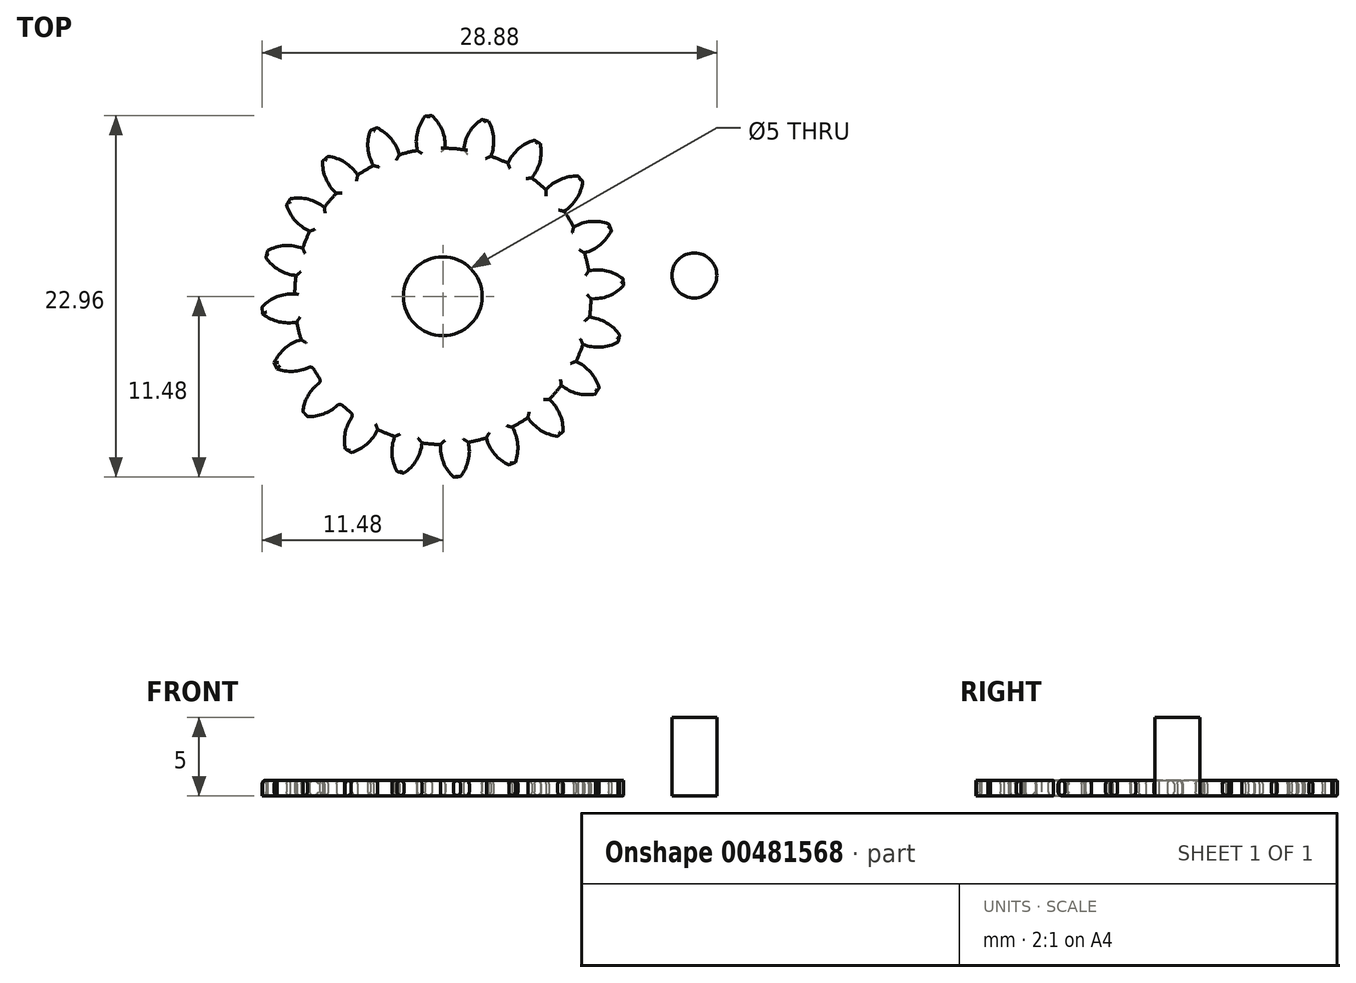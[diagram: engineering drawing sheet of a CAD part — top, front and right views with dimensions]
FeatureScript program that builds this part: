
annotation { "Feature Type Name" : "Feature", "Feature Type Description" : "" }
export const myFeature = defineFeature(function(context is Context, id is Id, definition is map)
    precondition{}
    {
        {
            assignVariable(context, id + "F0", {"name" : "GearDepth", "anyValue" : 1});
        }
        {
            assignVariable(context, id + "F1", {"name" : "TeethFillet", "anyValue" : getVariable(context, 'GearDepth') * .25});
        }
        {
            var Q0;
            Q0=qCreatedBy(makeId("Top.planeOp"),FACE);
            var sketch = newSketch(context, id + "F2", { "sketchPlane" : qUnion([Q0])});
            skCircle(sketch, "E0", {"center": v(0, 0) * mm, "radius": 9.4 * mm});
            skCircle(sketch, "E1", {"center": v(0, 0) * mm, "radius": 10.45 * mm, "construction": true});
            skCircle(sketch, "E2", {"center": v(0, 0) * mm, "radius": 11.5 * mm, "construction": true});
            skLineSegment(sketch, "E3", {"start": v(0, 0) * mm, "end": v(0, 17.6) * mm, "construction": true});
            skLineSegment(sketch, "E4", {"start": v(0, 0) * mm, "end": v(-1.42, 18) * mm, "construction": true});
            skLineSegment(sketch, "E5", {"start": v(0, 10.45) * mm, "end": v(-10.54, 10.45) * mm, "construction": true});
            skLineSegment(sketch, "E6", {"start": v(0, 10.45) * mm, "end": v(-10.3, 6.7) * mm, "construction": true});
            skCircle(sketch, "E7", {"center": v(0, 10.45) * mm, "radius": 2.61 * mm, "construction": true});
            skCircle(sketch, "E8", {"center": v(-2.46, 9.56) * mm, "radius": 2.61 * mm, "construction": true});
            skArc(sketch, "E9", {"start": v(-4.91, 10.45) * mm, "mid": v(-4.92, 10.42) * mm, "end": v(-4.94, 10.39) * mm});
            skArc(sketch, "E10.trimOffspring", {"start": v(0.15, 9.4) * mm, "mid": v(-0.03, 10.54) * mm, "end": v(-0.68, 11.48) * mm});
            skArc(sketch, "E11.MirrorCS", {"start": v(-1.62, 9.27) * mm, "mid": v(-1.62, 10.41) * mm, "end": v(-1.12, 11.45) * mm});
            skLineSegment(sketch, "E12", {"start": v(-1.12, 11.45) * mm, "end": v(-0.68, 11.48) * mm});
            skArc(sketch, "E13.1.0", {"start": v(-2.76, 9) * mm, "mid": v(-3.29, 10.01) * mm, "end": v(-4.2, 10.7) * mm});
            skLineSegment(sketch, "E13.1.1", {"start": v(-4.6, 10.54) * mm, "end": v(-4.2, 10.7) * mm});
            skArc(sketch, "E13.1.2", {"start": v(-4.4, 8.31) * mm, "mid": v(-4.76, 9.4) * mm, "end": v(-4.6, 10.54) * mm});
            skArc(sketch, "E13.2.0", {"start": v(-5.4, 7.7) * mm, "mid": v(-6.22, 8.5) * mm, "end": v(-7.3, 8.89) * mm});
            skLineSegment(sketch, "E13.2.1", {"start": v(-7.64, 8.6) * mm, "end": v(-7.3, 8.89) * mm});
            skArc(sketch, "E13.2.2", {"start": v(-6.76, 6.54) * mm, "mid": v(-7.43, 7.47) * mm, "end": v(-7.64, 8.6) * mm});
            skArc(sketch, "E13.3.0", {"start": v(-7.52, 5.65) * mm, "mid": v(-8.54, 6.17) * mm, "end": v(-9.69, 6.2) * mm});
            skLineSegment(sketch, "E13.3.1", {"start": v(-9.92, 5.82) * mm, "end": v(-9.69, 6.2) * mm});
            skArc(sketch, "E13.3.2", {"start": v(-8.45, 4.13) * mm, "mid": v(-9.37, 4.81) * mm, "end": v(-9.92, 5.82) * mm});
            skArc(sketch, "E13.4.0", {"start": v(-8.9, 3.05) * mm, "mid": v(-10.03, 3.23) * mm, "end": v(-11.13, 2.9) * mm});
            skLineSegment(sketch, "E13.4.1", {"start": v(-11.23, 2.47) * mm, "end": v(-11.13, 2.9) * mm});
            skArc(sketch, "E13.4.2", {"start": v(-9.32, 1.32) * mm, "mid": v(-10.4, 1.68) * mm, "end": v(-11.23, 2.47) * mm});
            skArc(sketch, "E13.5.0", {"start": v(-9.4, 0.15) * mm, "mid": v(-10.54, -0.03) * mm, "end": v(-11.48, -0.68) * mm});
            skLineSegment(sketch, "E13.5.1", {"start": v(-11.45, -1.12) * mm, "end": v(-11.48, -0.68) * mm});
            skArc(sketch, "E13.5.2", {"start": v(-9.27, -1.62) * mm, "mid": v(-10.41, -1.62) * mm, "end": v(-11.45, -1.12) * mm});
            skArc(sketch, "E13.6.0", {"start": v(-9, -2.76) * mm, "mid": v(-10.01, -3.29) * mm, "end": v(-10.7, -4.2) * mm});
            skLineSegment(sketch, "E13.6.1", {"start": v(-10.54, -4.6) * mm, "end": v(-10.7, -4.2) * mm});
            skArc(sketch, "E13.6.2", {"start": v(-8.31, -4.4) * mm, "mid": v(-9.4, -4.76) * mm, "end": v(-10.54, -4.6) * mm});
            skArc(sketch, "E13.7.0", {"start": v(-7.7, -5.4) * mm, "mid": v(-8.5, -6.22) * mm, "end": v(-8.89, -7.3) * mm});
            skLineSegment(sketch, "E13.7.1", {"start": v(-8.6, -7.64) * mm, "end": v(-8.89, -7.3) * mm});
            skArc(sketch, "E13.7.2", {"start": v(-6.54, -6.76) * mm, "mid": v(-7.47, -7.43) * mm, "end": v(-8.6, -7.64) * mm});
            skArc(sketch, "E13.8.0", {"start": v(-5.65, -7.52) * mm, "mid": v(-6.17, -8.54) * mm, "end": v(-6.2, -9.69) * mm});
            skLineSegment(sketch, "E13.8.1", {"start": v(-5.82, -9.92) * mm, "end": v(-6.2, -9.69) * mm});
            skArc(sketch, "E13.8.2", {"start": v(-4.13, -8.45) * mm, "mid": v(-4.81, -9.37) * mm, "end": v(-5.82, -9.92) * mm});
            skArc(sketch, "E13.9.0", {"start": v(-3.05, -8.9) * mm, "mid": v(-3.23, -10.03) * mm, "end": v(-2.9, -11.13) * mm});
            skLineSegment(sketch, "E13.9.1", {"start": v(-2.47, -11.23) * mm, "end": v(-2.9, -11.13) * mm});
            skArc(sketch, "E13.9.2", {"start": v(-1.32, -9.32) * mm, "mid": v(-1.68, -10.4) * mm, "end": v(-2.47, -11.23) * mm});
            skArc(sketch, "E13.10.0", {"start": v(-0.15, -9.4) * mm, "mid": v(0.03, -10.54) * mm, "end": v(0.68, -11.48) * mm});
            skLineSegment(sketch, "E13.10.1", {"start": v(1.12, -11.45) * mm, "end": v(0.68, -11.48) * mm});
            skArc(sketch, "E13.10.2", {"start": v(1.62, -9.27) * mm, "mid": v(1.62, -10.41) * mm, "end": v(1.12, -11.45) * mm});
            skArc(sketch, "E13.11.0", {"start": v(2.76, -9) * mm, "mid": v(3.29, -10.01) * mm, "end": v(4.2, -10.7) * mm});
            skLineSegment(sketch, "E13.11.1", {"start": v(4.6, -10.54) * mm, "end": v(4.2, -10.7) * mm});
            skArc(sketch, "E13.11.2", {"start": v(4.4, -8.31) * mm, "mid": v(4.76, -9.4) * mm, "end": v(4.6, -10.54) * mm});
            skArc(sketch, "E13.12.0", {"start": v(5.4, -7.7) * mm, "mid": v(6.22, -8.5) * mm, "end": v(7.3, -8.89) * mm});
            skLineSegment(sketch, "E13.12.1", {"start": v(7.64, -8.6) * mm, "end": v(7.3, -8.89) * mm});
            skArc(sketch, "E13.12.2", {"start": v(6.76, -6.54) * mm, "mid": v(7.43, -7.47) * mm, "end": v(7.64, -8.6) * mm});
            skArc(sketch, "E13.13.0", {"start": v(7.52, -5.65) * mm, "mid": v(8.54, -6.17) * mm, "end": v(9.69, -6.2) * mm});
            skLineSegment(sketch, "E13.13.1", {"start": v(9.92, -5.82) * mm, "end": v(9.69, -6.2) * mm});
            skArc(sketch, "E13.13.2", {"start": v(8.45, -4.13) * mm, "mid": v(9.37, -4.81) * mm, "end": v(9.92, -5.82) * mm});
            skArc(sketch, "E13.14.0", {"start": v(8.9, -3.05) * mm, "mid": v(10.03, -3.23) * mm, "end": v(11.13, -2.9) * mm});
            skLineSegment(sketch, "E13.14.1", {"start": v(11.23, -2.47) * mm, "end": v(11.13, -2.9) * mm});
            skArc(sketch, "E13.14.2", {"start": v(9.32, -1.32) * mm, "mid": v(10.4, -1.68) * mm, "end": v(11.23, -2.47) * mm});
            skArc(sketch, "E13.15.0", {"start": v(9.4, -0.15) * mm, "mid": v(10.54, 0.03) * mm, "end": v(11.48, 0.68) * mm});
            skLineSegment(sketch, "E13.15.1", {"start": v(11.45, 1.12) * mm, "end": v(11.48, 0.68) * mm});
            skArc(sketch, "E13.15.2", {"start": v(9.27, 1.62) * mm, "mid": v(10.41, 1.62) * mm, "end": v(11.45, 1.12) * mm});
            skArc(sketch, "E13.16.0", {"start": v(9, 2.76) * mm, "mid": v(10.01, 3.29) * mm, "end": v(10.7, 4.2) * mm});
            skLineSegment(sketch, "E13.16.1", {"start": v(10.54, 4.6) * mm, "end": v(10.7, 4.2) * mm});
            skArc(sketch, "E13.16.2", {"start": v(8.31, 4.4) * mm, "mid": v(9.4, 4.76) * mm, "end": v(10.54, 4.6) * mm});
            skArc(sketch, "E13.17.0", {"start": v(7.7, 5.4) * mm, "mid": v(8.5, 6.22) * mm, "end": v(8.89, 7.3) * mm});
            skLineSegment(sketch, "E13.17.1", {"start": v(8.6, 7.64) * mm, "end": v(8.89, 7.3) * mm});
            skArc(sketch, "E13.17.2", {"start": v(6.54, 6.76) * mm, "mid": v(7.47, 7.43) * mm, "end": v(8.6, 7.64) * mm});
            skArc(sketch, "E13.18.0", {"start": v(5.65, 7.52) * mm, "mid": v(6.17, 8.54) * mm, "end": v(6.2, 9.69) * mm});
            skLineSegment(sketch, "E13.18.1", {"start": v(5.82, 9.92) * mm, "end": v(6.2, 9.69) * mm});
            skArc(sketch, "E13.18.2", {"start": v(4.13, 8.45) * mm, "mid": v(4.81, 9.37) * mm, "end": v(5.82, 9.92) * mm});
            skArc(sketch, "E13.19.0", {"start": v(3.05, 8.9) * mm, "mid": v(3.23, 10.03) * mm, "end": v(2.9, 11.13) * mm});
            skLineSegment(sketch, "E13.19.1", {"start": v(2.47, 11.23) * mm, "end": v(2.9, 11.13) * mm});
            skArc(sketch, "E13.19.2", {"start": v(1.32, 9.32) * mm, "mid": v(1.68, 10.4) * mm, "end": v(2.47, 11.23) * mm});
            skCircle(sketch, "E14", {"center": v(0, 0) * mm, "radius": 2.5 * mm});
            skSolve(sketch);
        }
        {
            var Q0;
            {var subQ0=sQuery(id+"F2.wireOp",EDGE,"E10.trimOffspring");Q0=makeQuery(id+"F2.imprint","IMPRINT",FACE,{"disambiguationData":[TD([[makeQuery(id+"F2.imprint","IMPRINT",EDGE,{"derivedFrom":subQ0}),1.0]])]});}
            var Q1;
            {var subQ0=sQuery(id+"F2.wireOp",EDGE,"E0");var subQ1=makeQuery(id+"F2.imprint","INTERSECT",VERTEX,{"derivedFrom":[subQ0,sQuery(id+"F2.wireOp",EDGE,"E10.trimOffspring")]});Q1=makeQuery(id+"F2.imprint","IMPRINT",FACE,{"disambiguationData":[TD([[makeQuery(id+"F2.imprint","IMPRINT",EDGE,{"disambiguationData":[TD([[subQ1,-1.0]])],"derivedFrom":subQ0}),1.0]])]});}
            var Q2;
            {var subQ0=sQuery(id+"F2.wireOp",EDGE,"E13.1.0");Q2=makeQuery(id+"F2.imprint","IMPRINT",FACE,{"disambiguationData":[TD([[makeQuery(id+"F2.imprint","IMPRINT",EDGE,{"derivedFrom":subQ0}),1.0]])]});}
            var Q3;
            {var subQ0=sQuery(id+"F2.wireOp",EDGE,"E13.2.0");Q3=makeQuery(id+"F2.imprint","IMPRINT",FACE,{"disambiguationData":[TD([[makeQuery(id+"F2.imprint","IMPRINT",EDGE,{"derivedFrom":subQ0}),1.0]])]});}
            var Q4;
            {var subQ0=sQuery(id+"F2.wireOp",EDGE,"E13.3.0");Q4=makeQuery(id+"F2.imprint","IMPRINT",FACE,{"disambiguationData":[TD([[makeQuery(id+"F2.imprint","IMPRINT",EDGE,{"derivedFrom":subQ0}),1.0]])]});}
            var Q5;
            {var subQ0=sQuery(id+"F2.wireOp",EDGE,"E13.4.0");Q5=makeQuery(id+"F2.imprint","IMPRINT",FACE,{"disambiguationData":[TD([[makeQuery(id+"F2.imprint","IMPRINT",EDGE,{"derivedFrom":subQ0}),1.0]])]});}
            var Q6;
            {var subQ0=sQuery(id+"F2.wireOp",EDGE,"E13.5.0");Q6=makeQuery(id+"F2.imprint","IMPRINT",FACE,{"disambiguationData":[TD([[makeQuery(id+"F2.imprint","IMPRINT",EDGE,{"derivedFrom":subQ0}),1.0]])]});}
            var Q7;
            {var subQ0=sQuery(id+"F2.wireOp",EDGE,"E13.6.0");Q7=makeQuery(id+"F2.imprint","IMPRINT",FACE,{"disambiguationData":[TD([[makeQuery(id+"F2.imprint","IMPRINT",EDGE,{"derivedFrom":subQ0}),1.0]])]});}
            var Q8;
            {var subQ0=sQuery(id+"F2.wireOp",EDGE,"E13.7.0");Q8=makeQuery(id+"F2.imprint","IMPRINT",FACE,{"disambiguationData":[TD([[makeQuery(id+"F2.imprint","IMPRINT",EDGE,{"derivedFrom":subQ0}),1.0]])]});}
            var Q9;
            {var subQ0=sQuery(id+"F2.wireOp",EDGE,"E13.8.0");Q9=makeQuery(id+"F2.imprint","IMPRINT",FACE,{"disambiguationData":[TD([[makeQuery(id+"F2.imprint","IMPRINT",EDGE,{"derivedFrom":subQ0}),1.0]])]});}
            var Q10;
            {var subQ0=sQuery(id+"F2.wireOp",EDGE,"E13.9.0");Q10=makeQuery(id+"F2.imprint","IMPRINT",FACE,{"disambiguationData":[TD([[makeQuery(id+"F2.imprint","IMPRINT",EDGE,{"derivedFrom":subQ0}),1.0]])]});}
            var Q11;
            {var subQ0=sQuery(id+"F2.wireOp",EDGE,"E13.10.0");Q11=makeQuery(id+"F2.imprint","IMPRINT",FACE,{"disambiguationData":[TD([[makeQuery(id+"F2.imprint","IMPRINT",EDGE,{"derivedFrom":subQ0}),1.0]])]});}
            var Q12;
            {var subQ0=sQuery(id+"F2.wireOp",EDGE,"E13.11.0");Q12=makeQuery(id+"F2.imprint","IMPRINT",FACE,{"disambiguationData":[TD([[makeQuery(id+"F2.imprint","IMPRINT",EDGE,{"derivedFrom":subQ0}),1.0]])]});}
            var Q13;
            {var subQ0=sQuery(id+"F2.wireOp",EDGE,"E13.12.0");Q13=makeQuery(id+"F2.imprint","IMPRINT",FACE,{"disambiguationData":[TD([[makeQuery(id+"F2.imprint","IMPRINT",EDGE,{"derivedFrom":subQ0}),1.0]])]});}
            var Q14;
            {var subQ0=sQuery(id+"F2.wireOp",EDGE,"E13.13.0");Q14=makeQuery(id+"F2.imprint","IMPRINT",FACE,{"disambiguationData":[TD([[makeQuery(id+"F2.imprint","IMPRINT",EDGE,{"derivedFrom":subQ0}),1.0]])]});}
            var Q15;
            {var subQ0=sQuery(id+"F2.wireOp",EDGE,"E13.14.0");Q15=makeQuery(id+"F2.imprint","IMPRINT",FACE,{"disambiguationData":[TD([[makeQuery(id+"F2.imprint","IMPRINT",EDGE,{"derivedFrom":subQ0}),1.0]])]});}
            var Q16;
            {var subQ0=sQuery(id+"F2.wireOp",EDGE,"E13.15.0");Q16=makeQuery(id+"F2.imprint","IMPRINT",FACE,{"disambiguationData":[TD([[makeQuery(id+"F2.imprint","IMPRINT",EDGE,{"derivedFrom":subQ0}),1.0]])]});}
            var Q17;
            {var subQ0=sQuery(id+"F2.wireOp",EDGE,"E13.16.0");Q17=makeQuery(id+"F2.imprint","IMPRINT",FACE,{"disambiguationData":[TD([[makeQuery(id+"F2.imprint","IMPRINT",EDGE,{"derivedFrom":subQ0}),1.0]])]});}
            var Q18;
            {var subQ0=sQuery(id+"F2.wireOp",EDGE,"E13.17.0");Q18=makeQuery(id+"F2.imprint","IMPRINT",FACE,{"disambiguationData":[TD([[makeQuery(id+"F2.imprint","IMPRINT",EDGE,{"derivedFrom":subQ0}),1.0]])]});}
            var Q19;
            {var subQ0=sQuery(id+"F2.wireOp",EDGE,"E13.18.0");Q19=makeQuery(id+"F2.imprint","IMPRINT",FACE,{"disambiguationData":[TD([[makeQuery(id+"F2.imprint","IMPRINT",EDGE,{"derivedFrom":subQ0}),1.0]])]});}
            var Q20;
            {var subQ0=sQuery(id+"F2.wireOp",EDGE,"E13.19.0");Q20=makeQuery(id+"F2.imprint","IMPRINT",FACE,{"disambiguationData":[TD([[makeQuery(id+"F2.imprint","IMPRINT",EDGE,{"derivedFrom":subQ0}),1.0]])]});}
            var Q21;
            Q21=sQuery(id+"F2.wireOp",EDGE,"E0");
            var Q22;
            Q22=sQuery(id+"F2.wireOp",EDGE,"E10.trimOffspring");
            var Q23;
            Q23=sQuery(id+"F2.wireOp",EDGE,"E12");
            var Q24;
            Q24=sQuery(id+"F2.wireOp",EDGE,"E11.MirrorCS");
            extrude(context, id + "F3", {"entities" : qUnion([Q0, Q1, Q2, Q3, Q4, Q5, Q6, Q7, Q8, Q9, Q10, Q11, Q12, Q13, Q14, Q15, Q16, Q17, Q18, Q19, Q20]), "surfaceEntities" : qUnion([Q21, Q22, Q23, Q24]), "depth" : (getVariable(context, 'GearDepth')) * mm});
        }
        {
            var Q0;
            Q0=qCreatedBy(makeId("Top.planeOp"),FACE);
            var sketch = newSketch(context, id + "F4", { "sketchPlane" : qUnion([Q0])});
            skCircle(sketch, "E15", {"center": v(15.97, 1.33) * mm, "radius": 1.43 * mm});
            skSolve(sketch);
        }
        {
            var Q0;
            Q0=makeQuery(id+"F4.imprint","IMPRINT",FACE,{"disambiguationData":[TD([[makeQuery(id+"F4.imprint","IMPRINT",EDGE,{"derivedFrom":sQuery(id+"F4.wireOp",EDGE,"E15")}),1.0]])]});
            extrude(context, id + "F5", {"entities" : qUnion([Q0]), "depth" : 5 * mm});
        }
        {
            var Q0;
            Q0=makeQuery(id+"F3.opExtrude","CAP_EDGE",EDGE,{"disambiguationData":[OSD([sQuery(id+"F2.wireOp",EDGE,"E13.5.2")])],"isStart":false});
            var Q1;
            Q1=makeQuery(id+"F3.opExtrude","CAP_EDGE",EDGE,{"disambiguationData":[OSD([sQuery(id+"F2.wireOp",EDGE,"E13.5.1")])],"isStart":false});
            var Q2;
            {var subQ0=sQuery(id+"F2.wireOp",EDGE,"E0");Q2=makeQuery(id+"F3.opExtrude","CAP_EDGE",EDGE,{"disambiguationData":[OSD([subQ0]),TDD([makeQuery(id+"F2.imprint","IMPRINT",EDGE,{"disambiguationData":[TD([[makeQuery(id+"F2.imprint","INTERSECT",VERTEX,{"derivedFrom":[subQ0,sQuery(id+"F2.wireOp",EDGE,"E13.5.2")]}),-1.0]])],"derivedFrom":subQ0})])],"isStart":false});}
            var Q3;
            Q3=makeQuery(id+"F3.opExtrude","CAP_EDGE",EDGE,{"disambiguationData":[OSD([sQuery(id+"F2.wireOp",EDGE,"E13.6.0")])],"isStart":false});
            var Q4;
            Q4=makeQuery(id+"F3.opExtrude","CAP_EDGE",EDGE,{"disambiguationData":[OSD([sQuery(id+"F2.wireOp",EDGE,"E13.6.1")])],"isStart":false});
            var Q5;
            Q5=makeQuery(id+"F3.opExtrude","CAP_EDGE",EDGE,{"disambiguationData":[OSD([sQuery(id+"F2.wireOp",EDGE,"E13.6.2")])],"isStart":false});
            var Q6;
            {var subQ0=sQuery(id+"F2.wireOp",EDGE,"E0");Q6=makeQuery(id+"F3.opExtrude","SWEPT_FACE",FACE,{"disambiguationData":[OSD([subQ0]),TDD([makeQuery(id+"F2.imprint","IMPRINT",EDGE,{"disambiguationData":[TD([[makeQuery(id+"F2.imprint","INTERSECT",VERTEX,{"derivedFrom":[subQ0,sQuery(id+"F2.wireOp",EDGE,"E13.6.2")]}),-1.0]])],"derivedFrom":subQ0})])]});}
            var Q7;
            {var subQ0=sQuery(id+"F2.wireOp",EDGE,"E0");Q7=makeQuery(id+"F3.opExtrude","CAP_EDGE",EDGE,{"disambiguationData":[OSD([subQ0]),TDD([makeQuery(id+"F2.imprint","IMPRINT",EDGE,{"disambiguationData":[TD([[makeQuery(id+"F2.imprint","INTERSECT",VERTEX,{"derivedFrom":[subQ0,sQuery(id+"F2.wireOp",EDGE,"E13.6.2")]}),-1.0]])],"derivedFrom":subQ0})])],"isStart":false});}
            var Q8;
            Q8=makeQuery(id+"F3.opExtrude","CAP_EDGE",EDGE,{"disambiguationData":[OSD([sQuery(id+"F2.wireOp",EDGE,"E13.7.2")])],"isStart":true});
            var Q9;
            {var subQ0=sQuery(id+"F2.wireOp",EDGE,"E0");Q9=makeQuery(id+"F3.opExtrude","CAP_EDGE",EDGE,{"disambiguationData":[OSD([subQ0]),TDD([makeQuery(id+"F2.imprint","IMPRINT",EDGE,{"disambiguationData":[TD([[makeQuery(id+"F2.imprint","INTERSECT",VERTEX,{"derivedFrom":[subQ0,sQuery(id+"F2.wireOp",EDGE,"E13.7.2")]}),-1.0]])],"derivedFrom":subQ0})])],"isStart":true});}
            var Q10;
            Q10=makeQuery(id+"F3.opExtrude","CAP_EDGE",EDGE,{"disambiguationData":[OSD([sQuery(id+"F2.wireOp",EDGE,"E13.7.2")])],"isStart":false});
            var Q11;
            {var subQ0=sQuery(id+"F2.wireOp",EDGE,"E0");Q11=makeQuery(id+"F3.opExtrude","CAP_EDGE",EDGE,{"disambiguationData":[OSD([subQ0]),TDD([makeQuery(id+"F2.imprint","IMPRINT",EDGE,{"disambiguationData":[TD([[makeQuery(id+"F2.imprint","INTERSECT",VERTEX,{"derivedFrom":[subQ0,sQuery(id+"F2.wireOp",EDGE,"E13.7.2")]}),-1.0]])],"derivedFrom":subQ0})])],"isStart":false});}
            var Q12;
            Q12=makeQuery(id+"F3.opExtrude","CAP_EDGE",EDGE,{"disambiguationData":[OSD([sQuery(id+"F2.wireOp",EDGE,"E13.8.0")])],"isStart":false});
            var Q13;
            {var subQ0=sQuery(id+"F2.wireOp",EDGE,"E0");Q13=makeQuery(id+"F3.opExtrude","SWEPT_FACE",FACE,{"disambiguationData":[OSD([subQ0]),TDD([makeQuery(id+"F2.imprint","IMPRINT",EDGE,{"disambiguationData":[TD([[makeQuery(id+"F2.imprint","INTERSECT",VERTEX,{"derivedFrom":[subQ0,sQuery(id+"F2.wireOp",EDGE,"E13.7.2")]}),-1.0]])],"derivedFrom":subQ0})])]});}
            var Q14;
            Q14=makeQuery(id+"F3.opExtrude","CAP_EDGE",EDGE,{"disambiguationData":[OSD([sQuery(id+"F2.wireOp",EDGE,"E13.6.0")])],"isStart":true});
            var Q15;
            Q15=makeQuery(id+"F3.opExtrude","CAP_EDGE",EDGE,{"disambiguationData":[OSD([sQuery(id+"F2.wireOp",EDGE,"E13.8.2")])],"isStart":false});
            var Q16;
            {var subQ0=sQuery(id+"F2.wireOp",EDGE,"E0");Q16=makeQuery(id+"F3.opExtrude","CAP_EDGE",EDGE,{"disambiguationData":[OSD([subQ0]),TDD([makeQuery(id+"F2.imprint","IMPRINT",EDGE,{"disambiguationData":[TD([[makeQuery(id+"F2.imprint","INTERSECT",VERTEX,{"derivedFrom":[subQ0,sQuery(id+"F2.wireOp",EDGE,"E13.8.2")]}),-1.0]])],"derivedFrom":subQ0})])],"isStart":false});}
            var Q17;
            Q17=makeQuery(id+"F3.opExtrude","CAP_EDGE",EDGE,{"disambiguationData":[OSD([sQuery(id+"F2.wireOp",EDGE,"E13.9.0")])],"isStart":false});
            var Q18;
            Q18=makeQuery(id+"F3.opExtrude","CAP_EDGE",EDGE,{"disambiguationData":[OSD([sQuery(id+"F2.wireOp",EDGE,"E13.9.2")])],"isStart":false});
            var Q19;
            {var subQ0=sQuery(id+"F2.wireOp",EDGE,"E0");Q19=makeQuery(id+"F3.opExtrude","CAP_EDGE",EDGE,{"disambiguationData":[OSD([subQ0]),TDD([makeQuery(id+"F2.imprint","IMPRINT",EDGE,{"disambiguationData":[TD([[makeQuery(id+"F2.imprint","INTERSECT",VERTEX,{"derivedFrom":[subQ0,sQuery(id+"F2.wireOp",EDGE,"E13.9.2")]}),-1.0]])],"derivedFrom":subQ0})])],"isStart":false});}
            var Q20;
            Q20=makeQuery(id+"F3.opExtrude","CAP_EDGE",EDGE,{"disambiguationData":[OSD([sQuery(id+"F2.wireOp",EDGE,"E13.10.0")])],"isStart":false});
            var Q21;
            Q21=makeQuery(id+"F3.opExtrude","CAP_EDGE",EDGE,{"disambiguationData":[OSD([sQuery(id+"F2.wireOp",EDGE,"E13.10.2")])],"isStart":false});
            var Q22;
            {var subQ0=sQuery(id+"F2.wireOp",EDGE,"E0");Q22=makeQuery(id+"F3.opExtrude","CAP_EDGE",EDGE,{"disambiguationData":[OSD([subQ0]),TDD([makeQuery(id+"F2.imprint","IMPRINT",EDGE,{"disambiguationData":[TD([[makeQuery(id+"F2.imprint","INTERSECT",VERTEX,{"derivedFrom":[subQ0,sQuery(id+"F2.wireOp",EDGE,"E13.10.2")]}),-1.0]])],"derivedFrom":subQ0})])],"isStart":false});}
            var Q23;
            Q23=makeQuery(id+"F3.opExtrude","CAP_EDGE",EDGE,{"disambiguationData":[OSD([sQuery(id+"F2.wireOp",EDGE,"E13.11.0")])],"isStart":false});
            var Q24;
            Q24=makeQuery(id+"F3.opExtrude","CAP_EDGE",EDGE,{"disambiguationData":[OSD([sQuery(id+"F2.wireOp",EDGE,"E13.11.2")])],"isStart":false});
            var Q25;
            {var subQ0=sQuery(id+"F2.wireOp",EDGE,"E0");Q25=makeQuery(id+"F3.opExtrude","CAP_EDGE",EDGE,{"disambiguationData":[OSD([subQ0]),TDD([makeQuery(id+"F2.imprint","IMPRINT",EDGE,{"disambiguationData":[TD([[makeQuery(id+"F2.imprint","INTERSECT",VERTEX,{"derivedFrom":[subQ0,sQuery(id+"F2.wireOp",EDGE,"E13.11.2")]}),-1.0]])],"derivedFrom":subQ0})])],"isStart":false});}
            var Q26;
            Q26=makeQuery(id+"F3.opExtrude","CAP_EDGE",EDGE,{"disambiguationData":[OSD([sQuery(id+"F2.wireOp",EDGE,"E13.12.0")])],"isStart":false});
            var Q27;
            Q27=makeQuery(id+"F3.opExtrude","CAP_EDGE",EDGE,{"disambiguationData":[OSD([sQuery(id+"F2.wireOp",EDGE,"E13.12.2")])],"isStart":false});
            var Q28;
            {var subQ0=sQuery(id+"F2.wireOp",EDGE,"E0");Q28=makeQuery(id+"F3.opExtrude","CAP_EDGE",EDGE,{"disambiguationData":[OSD([subQ0]),TDD([makeQuery(id+"F2.imprint","IMPRINT",EDGE,{"disambiguationData":[TD([[makeQuery(id+"F2.imprint","INTERSECT",VERTEX,{"derivedFrom":[subQ0,sQuery(id+"F2.wireOp",EDGE,"E13.12.2")]}),-1.0]])],"derivedFrom":subQ0})])],"isStart":false});}
            var Q29;
            Q29=makeQuery(id+"F3.opExtrude","CAP_EDGE",EDGE,{"disambiguationData":[OSD([sQuery(id+"F2.wireOp",EDGE,"E13.13.0")])],"isStart":false});
            var Q30;
            Q30=makeQuery(id+"F3.opExtrude","CAP_EDGE",EDGE,{"disambiguationData":[OSD([sQuery(id+"F2.wireOp",EDGE,"E13.13.2")])],"isStart":false});
            var Q31;
            {var subQ0=sQuery(id+"F2.wireOp",EDGE,"E0");Q31=makeQuery(id+"F3.opExtrude","CAP_EDGE",EDGE,{"disambiguationData":[OSD([subQ0]),TDD([makeQuery(id+"F2.imprint","IMPRINT",EDGE,{"disambiguationData":[TD([[makeQuery(id+"F2.imprint","INTERSECT",VERTEX,{"derivedFrom":[subQ0,sQuery(id+"F2.wireOp",EDGE,"E13.13.2")]}),-1.0]])],"derivedFrom":subQ0})])],"isStart":false});}
            var Q32;
            Q32=makeQuery(id+"F3.opExtrude","CAP_EDGE",EDGE,{"disambiguationData":[OSD([sQuery(id+"F2.wireOp",EDGE,"E13.14.0")])],"isStart":false});
            var Q33;
            Q33=makeQuery(id+"F3.opExtrude","CAP_EDGE",EDGE,{"disambiguationData":[OSD([sQuery(id+"F2.wireOp",EDGE,"E13.14.2")])],"isStart":false});
            var Q34;
            {var subQ0=sQuery(id+"F2.wireOp",EDGE,"E0");Q34=makeQuery(id+"F3.opExtrude","CAP_EDGE",EDGE,{"disambiguationData":[OSD([subQ0]),TDD([makeQuery(id+"F2.imprint","IMPRINT",EDGE,{"disambiguationData":[TD([[makeQuery(id+"F2.imprint","INTERSECT",VERTEX,{"derivedFrom":[subQ0,sQuery(id+"F2.wireOp",EDGE,"E13.14.2")]}),-1.0]])],"derivedFrom":subQ0})])],"isStart":false});}
            var Q35;
            Q35=makeQuery(id+"F3.opExtrude","CAP_EDGE",EDGE,{"disambiguationData":[OSD([sQuery(id+"F2.wireOp",EDGE,"E13.15.0")])],"isStart":false});
            var Q36;
            {var subQ0=sQuery(id+"F2.wireOp",EDGE,"E0");Q36=makeQuery(id+"F3.opExtrude","CAP_EDGE",EDGE,{"disambiguationData":[OSD([subQ0]),TDD([makeQuery(id+"F2.imprint","IMPRINT",EDGE,{"disambiguationData":[TD([[makeQuery(id+"F2.imprint","INTERSECT",VERTEX,{"derivedFrom":[subQ0,sQuery(id+"F2.wireOp",EDGE,"E13.14.2")]}),-1.0]])],"derivedFrom":subQ0})])],"isStart":false});}
            var Q37;
            Q37=makeQuery(id+"F3.opExtrude","CAP_EDGE",EDGE,{"disambiguationData":[OSD([sQuery(id+"F2.wireOp",EDGE,"E13.15.2")])],"isStart":false});
            var Q38;
            {var subQ0=sQuery(id+"F2.wireOp",EDGE,"E0");Q38=makeQuery(id+"F3.opExtrude","CAP_EDGE",EDGE,{"disambiguationData":[OSD([subQ0]),TDD([makeQuery(id+"F2.imprint","IMPRINT",EDGE,{"disambiguationData":[TD([[makeQuery(id+"F2.imprint","INTERSECT",VERTEX,{"derivedFrom":[subQ0,sQuery(id+"F2.wireOp",EDGE,"E13.15.2")]}),-1.0]])],"derivedFrom":subQ0})])],"isStart":false});}
            var Q39;
            Q39=makeQuery(id+"F3.opExtrude","CAP_EDGE",EDGE,{"disambiguationData":[OSD([sQuery(id+"F2.wireOp",EDGE,"E13.16.0")])],"isStart":false});
            var Q40;
            Q40=makeQuery(id+"F3.opExtrude","CAP_EDGE",EDGE,{"disambiguationData":[OSD([sQuery(id+"F2.wireOp",EDGE,"E13.16.2")])],"isStart":false});
            var Q41;
            Q41=makeQuery(id+"F3.opExtrude","CAP_EDGE",EDGE,{"disambiguationData":[OSD([sQuery(id+"F2.wireOp",EDGE,"E13.17.0")])],"isStart":false});
            var Q42;
            {var subQ0=sQuery(id+"F2.wireOp",EDGE,"E0");Q42=makeQuery(id+"F3.opExtrude","CAP_EDGE",EDGE,{"disambiguationData":[OSD([subQ0]),TDD([makeQuery(id+"F2.imprint","IMPRINT",EDGE,{"disambiguationData":[TD([[makeQuery(id+"F2.imprint","INTERSECT",VERTEX,{"derivedFrom":[subQ0,sQuery(id+"F2.wireOp",EDGE,"E13.16.2")]}),-1.0]])],"derivedFrom":subQ0})])],"isStart":false});}
            var Q43;
            Q43=makeQuery(id+"F3.opExtrude","CAP_EDGE",EDGE,{"disambiguationData":[OSD([sQuery(id+"F2.wireOp",EDGE,"E13.17.2")])],"isStart":false});
            var Q44;
            {var subQ0=sQuery(id+"F2.wireOp",EDGE,"E0");Q44=makeQuery(id+"F3.opExtrude","CAP_EDGE",EDGE,{"disambiguationData":[OSD([subQ0]),TDD([makeQuery(id+"F2.imprint","IMPRINT",EDGE,{"disambiguationData":[TD([[makeQuery(id+"F2.imprint","INTERSECT",VERTEX,{"derivedFrom":[subQ0,sQuery(id+"F2.wireOp",EDGE,"E13.17.2")]}),-1.0]])],"derivedFrom":subQ0})])],"isStart":false});}
            var Q45;
            Q45=makeQuery(id+"F3.opExtrude","CAP_EDGE",EDGE,{"disambiguationData":[OSD([sQuery(id+"F2.wireOp",EDGE,"E13.18.0")])],"isStart":false});
            var Q46;
            Q46=makeQuery(id+"F3.opExtrude","CAP_EDGE",EDGE,{"disambiguationData":[OSD([sQuery(id+"F2.wireOp",EDGE,"E13.18.2")])],"isStart":false});
            var Q47;
            {var subQ0=sQuery(id+"F2.wireOp",EDGE,"E0");Q47=makeQuery(id+"F3.opExtrude","CAP_EDGE",EDGE,{"disambiguationData":[OSD([subQ0]),TDD([makeQuery(id+"F2.imprint","IMPRINT",EDGE,{"disambiguationData":[TD([[makeQuery(id+"F2.imprint","INTERSECT",VERTEX,{"derivedFrom":[subQ0,sQuery(id+"F2.wireOp",EDGE,"E13.18.2")]}),-1.0]])],"derivedFrom":subQ0})])],"isStart":false});}
            var Q48;
            Q48=makeQuery(id+"F3.opExtrude","CAP_EDGE",EDGE,{"disambiguationData":[OSD([sQuery(id+"F2.wireOp",EDGE,"E13.19.0")])],"isStart":false});
            var Q49;
            Q49=makeQuery(id+"F3.opExtrude","CAP_EDGE",EDGE,{"disambiguationData":[OSD([sQuery(id+"F2.wireOp",EDGE,"E13.19.2")])],"isStart":false});
            var Q50;
            Q50=makeQuery(id+"F3.opExtrude","CAP_EDGE",EDGE,{"disambiguationData":[OSD([sQuery(id+"F2.wireOp",EDGE,"E10.trimOffspring")])],"isStart":false});
            var Q51;
            Q51=makeQuery(id+"F3.opExtrude","CAP_EDGE",EDGE,{"disambiguationData":[OSD([sQuery(id+"F2.wireOp",EDGE,"E11.MirrorCS")])],"isStart":false});
            var Q52;
            {var subQ0=sQuery(id+"F2.wireOp",EDGE,"E0");Q52=makeQuery(id+"F3.opExtrude","CAP_EDGE",EDGE,{"disambiguationData":[OSD([subQ0]),TDD([makeQuery(id+"F2.imprint","IMPRINT",EDGE,{"disambiguationData":[TD([[makeQuery(id+"F2.imprint","INTERSECT",VERTEX,{"derivedFrom":[subQ0,sQuery(id+"F2.wireOp",EDGE,"E11.MirrorCS")]}),-1.0]])],"derivedFrom":subQ0})])],"isStart":false});}
            var Q53;
            Q53=makeQuery(id+"F3.opExtrude","CAP_EDGE",EDGE,{"disambiguationData":[OSD([sQuery(id+"F2.wireOp",EDGE,"E13.1.0")])],"isStart":false});
            var Q54;
            Q54=makeQuery(id+"F3.opExtrude","CAP_EDGE",EDGE,{"disambiguationData":[OSD([sQuery(id+"F2.wireOp",EDGE,"E13.1.2")])],"isStart":false});
            var Q55;
            {var subQ0=sQuery(id+"F2.wireOp",EDGE,"E0");Q55=makeQuery(id+"F3.opExtrude","CAP_EDGE",EDGE,{"disambiguationData":[OSD([subQ0]),TDD([makeQuery(id+"F2.imprint","IMPRINT",EDGE,{"disambiguationData":[TD([[makeQuery(id+"F2.imprint","INTERSECT",VERTEX,{"derivedFrom":[subQ0,sQuery(id+"F2.wireOp",EDGE,"E13.1.2")]}),-1.0]])],"derivedFrom":subQ0})])],"isStart":false});}
            var Q56;
            Q56=makeQuery(id+"F3.opExtrude","CAP_EDGE",EDGE,{"disambiguationData":[OSD([sQuery(id+"F2.wireOp",EDGE,"E13.2.0")])],"isStart":false});
            var Q57;
            Q57=makeQuery(id+"F3.opExtrude","CAP_EDGE",EDGE,{"disambiguationData":[OSD([sQuery(id+"F2.wireOp",EDGE,"E13.2.2")])],"isStart":false});
            var Q58;
            {var subQ0=sQuery(id+"F2.wireOp",EDGE,"E0");Q58=makeQuery(id+"F3.opExtrude","CAP_EDGE",EDGE,{"disambiguationData":[OSD([subQ0]),TDD([makeQuery(id+"F2.imprint","IMPRINT",EDGE,{"disambiguationData":[TD([[makeQuery(id+"F2.imprint","INTERSECT",VERTEX,{"derivedFrom":[subQ0,sQuery(id+"F2.wireOp",EDGE,"E13.2.2")]}),-1.0]])],"derivedFrom":subQ0})])],"isStart":false});}
            var Q59;
            Q59=makeQuery(id+"F3.opExtrude","CAP_EDGE",EDGE,{"disambiguationData":[OSD([sQuery(id+"F2.wireOp",EDGE,"E13.3.0")])],"isStart":false});
            var Q60;
            Q60=makeQuery(id+"F3.opExtrude","CAP_EDGE",EDGE,{"disambiguationData":[OSD([sQuery(id+"F2.wireOp",EDGE,"E13.3.2")])],"isStart":false});
            var Q61;
            {var subQ0=sQuery(id+"F2.wireOp",EDGE,"E0");Q61=makeQuery(id+"F3.opExtrude","CAP_EDGE",EDGE,{"disambiguationData":[OSD([subQ0]),TDD([makeQuery(id+"F2.imprint","IMPRINT",EDGE,{"disambiguationData":[TD([[makeQuery(id+"F2.imprint","INTERSECT",VERTEX,{"derivedFrom":[subQ0,sQuery(id+"F2.wireOp",EDGE,"E13.3.2")]}),-1.0]])],"derivedFrom":subQ0})])],"isStart":false});}
            var Q62;
            Q62=makeQuery(id+"F3.opExtrude","CAP_EDGE",EDGE,{"disambiguationData":[OSD([sQuery(id+"F2.wireOp",EDGE,"E13.4.0")])],"isStart":false});
            var Q63;
            Q63=makeQuery(id+"F3.opExtrude","CAP_EDGE",EDGE,{"disambiguationData":[OSD([sQuery(id+"F2.wireOp",EDGE,"E13.4.2")])],"isStart":false});
            var Q64;
            {var subQ0=sQuery(id+"F2.wireOp",EDGE,"E0");Q64=makeQuery(id+"F3.opExtrude","CAP_EDGE",EDGE,{"disambiguationData":[OSD([subQ0]),TDD([makeQuery(id+"F2.imprint","IMPRINT",EDGE,{"disambiguationData":[TD([[makeQuery(id+"F2.imprint","INTERSECT",VERTEX,{"derivedFrom":[subQ0,sQuery(id+"F2.wireOp",EDGE,"E13.4.2")]}),-1.0]])],"derivedFrom":subQ0})])],"isStart":false});}
            var Q65;
            {var subQ0=sQuery(id+"F2.wireOp",EDGE,"E0");Q65=makeQuery(id+"F3.opExtrude","CAP_EDGE",EDGE,{"disambiguationData":[OSD([subQ0]),TDD([makeQuery(id+"F2.imprint","IMPRINT",EDGE,{"disambiguationData":[TD([[makeQuery(id+"F2.imprint","INTERSECT",VERTEX,{"derivedFrom":[subQ0,sQuery(id+"F2.wireOp",EDGE,"E13.5.2")]}),-1.0]])],"derivedFrom":subQ0})])],"isStart":true});}
            var Q66;
            Q66=makeQuery(id+"F3.opExtrude","CAP_EDGE",EDGE,{"disambiguationData":[OSD([sQuery(id+"F2.wireOp",EDGE,"E13.5.2")])],"isStart":true});
            var Q67;
            {var subQ0=sQuery(id+"F2.wireOp",EDGE,"E0");Q67=makeQuery(id+"F3.opExtrude","CAP_EDGE",EDGE,{"disambiguationData":[OSD([subQ0]),TDD([makeQuery(id+"F2.imprint","IMPRINT",EDGE,{"disambiguationData":[TD([[makeQuery(id+"F2.imprint","INTERSECT",VERTEX,{"derivedFrom":[subQ0,sQuery(id+"F2.wireOp",EDGE,"E13.4.2")]}),-1.0]])],"derivedFrom":subQ0})])],"isStart":true});}
            var Q68;
            Q68=makeQuery(id+"F3.opExtrude","CAP_EDGE",EDGE,{"disambiguationData":[OSD([sQuery(id+"F2.wireOp",EDGE,"E13.4.2")])],"isStart":true});
            var Q69;
            Q69=makeQuery(id+"F3.opExtrude","CAP_EDGE",EDGE,{"disambiguationData":[OSD([sQuery(id+"F2.wireOp",EDGE,"E13.4.0")])],"isStart":true});
            var Q70;
            {var subQ0=sQuery(id+"F2.wireOp",EDGE,"E0");Q70=makeQuery(id+"F3.opExtrude","CAP_EDGE",EDGE,{"disambiguationData":[OSD([subQ0]),TDD([makeQuery(id+"F2.imprint","IMPRINT",EDGE,{"disambiguationData":[TD([[makeQuery(id+"F2.imprint","INTERSECT",VERTEX,{"derivedFrom":[subQ0,sQuery(id+"F2.wireOp",EDGE,"E13.3.2")]}),-1.0]])],"derivedFrom":subQ0})])],"isStart":true});}
            var Q71;
            Q71=makeQuery(id+"F3.opExtrude","CAP_EDGE",EDGE,{"disambiguationData":[OSD([sQuery(id+"F2.wireOp",EDGE,"E13.3.2")])],"isStart":true});
            var Q72;
            Q72=makeQuery(id+"F3.opExtrude","CAP_EDGE",EDGE,{"disambiguationData":[OSD([sQuery(id+"F2.wireOp",EDGE,"E13.3.0")])],"isStart":true});
            var Q73;
            {var subQ0=sQuery(id+"F2.wireOp",EDGE,"E0");Q73=makeQuery(id+"F3.opExtrude","CAP_EDGE",EDGE,{"disambiguationData":[OSD([subQ0]),TDD([makeQuery(id+"F2.imprint","IMPRINT",EDGE,{"disambiguationData":[TD([[makeQuery(id+"F2.imprint","INTERSECT",VERTEX,{"derivedFrom":[subQ0,sQuery(id+"F2.wireOp",EDGE,"E13.2.2")]}),-1.0]])],"derivedFrom":subQ0})])],"isStart":true});}
            var Q74;
            Q74=makeQuery(id+"F3.opExtrude","CAP_EDGE",EDGE,{"disambiguationData":[OSD([sQuery(id+"F2.wireOp",EDGE,"E13.2.2")])],"isStart":true});
            var Q75;
            Q75=makeQuery(id+"F3.opExtrude","CAP_EDGE",EDGE,{"disambiguationData":[OSD([sQuery(id+"F2.wireOp",EDGE,"E13.2.0")])],"isStart":true});
            var Q76;
            Q76=makeQuery(id+"F3.opExtrude","CAP_EDGE",EDGE,{"disambiguationData":[OSD([sQuery(id+"F2.wireOp",EDGE,"E13.1.2")])],"isStart":true});
            var Q77;
            {var subQ0=sQuery(id+"F2.wireOp",EDGE,"E0");Q77=makeQuery(id+"F3.opExtrude","CAP_EDGE",EDGE,{"disambiguationData":[OSD([subQ0]),TDD([makeQuery(id+"F2.imprint","IMPRINT",EDGE,{"disambiguationData":[TD([[makeQuery(id+"F2.imprint","INTERSECT",VERTEX,{"derivedFrom":[subQ0,sQuery(id+"F2.wireOp",EDGE,"E13.1.2")]}),-1.0]])],"derivedFrom":subQ0})])],"isStart":true});}
            var Q78;
            Q78=makeQuery(id+"F3.opExtrude","CAP_EDGE",EDGE,{"disambiguationData":[OSD([sQuery(id+"F2.wireOp",EDGE,"E13.1.0")])],"isStart":true});
            var Q79;
            {var subQ0=sQuery(id+"F2.wireOp",EDGE,"E0");Q79=makeQuery(id+"F3.opExtrude","CAP_EDGE",EDGE,{"disambiguationData":[OSD([subQ0]),TDD([makeQuery(id+"F2.imprint","IMPRINT",EDGE,{"disambiguationData":[TD([[makeQuery(id+"F2.imprint","INTERSECT",VERTEX,{"derivedFrom":[subQ0,sQuery(id+"F2.wireOp",EDGE,"E11.MirrorCS")]}),-1.0]])],"derivedFrom":subQ0})])],"isStart":true});}
            var Q80;
            Q80=makeQuery(id+"F3.opExtrude","CAP_EDGE",EDGE,{"disambiguationData":[OSD([sQuery(id+"F2.wireOp",EDGE,"E11.MirrorCS")])],"isStart":true});
            var Q81;
            Q81=makeQuery(id+"F3.opExtrude","CAP_EDGE",EDGE,{"disambiguationData":[OSD([sQuery(id+"F2.wireOp",EDGE,"E10.trimOffspring")])],"isStart":true});
            var Q82;
            {var subQ0=sQuery(id+"F2.wireOp",EDGE,"E0");Q82=makeQuery(id+"F3.opExtrude","CAP_EDGE",EDGE,{"disambiguationData":[OSD([subQ0]),TDD([makeQuery(id+"F2.imprint","IMPRINT",EDGE,{"disambiguationData":[TD([[makeQuery(id+"F2.imprint","INTERSECT",VERTEX,{"derivedFrom":[subQ0,sQuery(id+"F2.wireOp",EDGE,"E10.trimOffspring")]}),1.0]])],"derivedFrom":subQ0})])],"isStart":true});}
            var Q83;
            Q83=makeQuery(id+"F3.opExtrude","CAP_EDGE",EDGE,{"disambiguationData":[OSD([sQuery(id+"F2.wireOp",EDGE,"E13.19.2")])],"isStart":true});
            var Q84;
            Q84=makeQuery(id+"F3.opExtrude","CAP_EDGE",EDGE,{"disambiguationData":[OSD([sQuery(id+"F2.wireOp",EDGE,"E13.19.0")])],"isStart":true});
            var Q85;
            {var subQ0=sQuery(id+"F2.wireOp",EDGE,"E0");Q85=makeQuery(id+"F3.opExtrude","CAP_EDGE",EDGE,{"disambiguationData":[OSD([subQ0]),TDD([makeQuery(id+"F2.imprint","IMPRINT",EDGE,{"disambiguationData":[TD([[makeQuery(id+"F2.imprint","INTERSECT",VERTEX,{"derivedFrom":[subQ0,sQuery(id+"F2.wireOp",EDGE,"E13.18.2")]}),-1.0]])],"derivedFrom":subQ0})])],"isStart":true});}
            var Q86;
            Q86=makeQuery(id+"F3.opExtrude","CAP_EDGE",EDGE,{"disambiguationData":[OSD([sQuery(id+"F2.wireOp",EDGE,"E13.18.2")])],"isStart":true});
            var Q87;
            Q87=makeQuery(id+"F3.opExtrude","CAP_EDGE",EDGE,{"disambiguationData":[OSD([sQuery(id+"F2.wireOp",EDGE,"E13.18.0")])],"isStart":true});
            var Q88;
            {var subQ0=sQuery(id+"F2.wireOp",EDGE,"E0");Q88=makeQuery(id+"F3.opExtrude","CAP_EDGE",EDGE,{"disambiguationData":[OSD([subQ0]),TDD([makeQuery(id+"F2.imprint","IMPRINT",EDGE,{"disambiguationData":[TD([[makeQuery(id+"F2.imprint","INTERSECT",VERTEX,{"derivedFrom":[subQ0,sQuery(id+"F2.wireOp",EDGE,"E13.17.2")]}),-1.0]])],"derivedFrom":subQ0})])],"isStart":true});}
            var Q89;
            Q89=makeQuery(id+"F3.opExtrude","CAP_EDGE",EDGE,{"disambiguationData":[OSD([sQuery(id+"F2.wireOp",EDGE,"E13.17.2")])],"isStart":true});
            var Q90;
            Q90=makeQuery(id+"F3.opExtrude","CAP_EDGE",EDGE,{"disambiguationData":[OSD([sQuery(id+"F2.wireOp",EDGE,"E13.17.0")])],"isStart":true});
            var Q91;
            {var subQ0=sQuery(id+"F2.wireOp",EDGE,"E0");Q91=makeQuery(id+"F3.opExtrude","CAP_EDGE",EDGE,{"disambiguationData":[OSD([subQ0]),TDD([makeQuery(id+"F2.imprint","IMPRINT",EDGE,{"disambiguationData":[TD([[makeQuery(id+"F2.imprint","INTERSECT",VERTEX,{"derivedFrom":[subQ0,sQuery(id+"F2.wireOp",EDGE,"E13.16.2")]}),-1.0]])],"derivedFrom":subQ0})])],"isStart":true});}
            var Q92;
            Q92=makeQuery(id+"F3.opExtrude","CAP_EDGE",EDGE,{"disambiguationData":[OSD([sQuery(id+"F2.wireOp",EDGE,"E13.16.2")])],"isStart":true});
            var Q93;
            Q93=makeQuery(id+"F3.opExtrude","CAP_EDGE",EDGE,{"disambiguationData":[OSD([sQuery(id+"F2.wireOp",EDGE,"E13.16.0")])],"isStart":true});
            var Q94;
            {var subQ0=sQuery(id+"F2.wireOp",EDGE,"E0");Q94=makeQuery(id+"F3.opExtrude","CAP_EDGE",EDGE,{"disambiguationData":[OSD([subQ0]),TDD([makeQuery(id+"F2.imprint","IMPRINT",EDGE,{"disambiguationData":[TD([[makeQuery(id+"F2.imprint","INTERSECT",VERTEX,{"derivedFrom":[subQ0,sQuery(id+"F2.wireOp",EDGE,"E13.15.2")]}),-1.0]])],"derivedFrom":subQ0})])],"isStart":true});}
            var Q95;
            Q95=makeQuery(id+"F3.opExtrude","CAP_EDGE",EDGE,{"disambiguationData":[OSD([sQuery(id+"F2.wireOp",EDGE,"E13.15.2")])],"isStart":true});
            var Q96;
            Q96=makeQuery(id+"F3.opExtrude","CAP_EDGE",EDGE,{"disambiguationData":[OSD([sQuery(id+"F2.wireOp",EDGE,"E13.15.0")])],"isStart":true});
            var Q97;
            {var subQ0=sQuery(id+"F2.wireOp",EDGE,"E0");Q97=makeQuery(id+"F3.opExtrude","CAP_EDGE",EDGE,{"disambiguationData":[OSD([subQ0]),TDD([makeQuery(id+"F2.imprint","IMPRINT",EDGE,{"disambiguationData":[TD([[makeQuery(id+"F2.imprint","INTERSECT",VERTEX,{"derivedFrom":[subQ0,sQuery(id+"F2.wireOp",EDGE,"E13.14.2")]}),-1.0]])],"derivedFrom":subQ0})])],"isStart":true});}
            var Q98;
            Q98=makeQuery(id+"F3.opExtrude","CAP_EDGE",EDGE,{"disambiguationData":[OSD([sQuery(id+"F2.wireOp",EDGE,"E13.14.2")])],"isStart":true});
            var Q99;
            Q99=makeQuery(id+"F3.opExtrude","CAP_EDGE",EDGE,{"disambiguationData":[OSD([sQuery(id+"F2.wireOp",EDGE,"E13.14.0")])],"isStart":true});
            var Q100;
            {var subQ0=sQuery(id+"F2.wireOp",EDGE,"E0");Q100=makeQuery(id+"F3.opExtrude","CAP_EDGE",EDGE,{"disambiguationData":[OSD([subQ0]),TDD([makeQuery(id+"F2.imprint","IMPRINT",EDGE,{"disambiguationData":[TD([[makeQuery(id+"F2.imprint","INTERSECT",VERTEX,{"derivedFrom":[subQ0,sQuery(id+"F2.wireOp",EDGE,"E13.13.2")]}),-1.0]])],"derivedFrom":subQ0})])],"isStart":true});}
            var Q101;
            Q101=makeQuery(id+"F3.opExtrude","CAP_EDGE",EDGE,{"disambiguationData":[OSD([sQuery(id+"F2.wireOp",EDGE,"E13.13.2")])],"isStart":true});
            var Q102;
            Q102=makeQuery(id+"F3.opExtrude","CAP_EDGE",EDGE,{"disambiguationData":[OSD([sQuery(id+"F2.wireOp",EDGE,"E13.13.0")])],"isStart":true});
            var Q103;
            {var subQ0=sQuery(id+"F2.wireOp",EDGE,"E0");Q103=makeQuery(id+"F3.opExtrude","CAP_EDGE",EDGE,{"disambiguationData":[OSD([subQ0]),TDD([makeQuery(id+"F2.imprint","IMPRINT",EDGE,{"disambiguationData":[TD([[makeQuery(id+"F2.imprint","INTERSECT",VERTEX,{"derivedFrom":[subQ0,sQuery(id+"F2.wireOp",EDGE,"E13.12.2")]}),-1.0]])],"derivedFrom":subQ0})])],"isStart":true});}
            var Q104;
            Q104=makeQuery(id+"F3.opExtrude","CAP_EDGE",EDGE,{"disambiguationData":[OSD([sQuery(id+"F2.wireOp",EDGE,"E13.12.2")])],"isStart":true});
            var Q105;
            Q105=makeQuery(id+"F3.opExtrude","CAP_EDGE",EDGE,{"disambiguationData":[OSD([sQuery(id+"F2.wireOp",EDGE,"E13.12.0")])],"isStart":true});
            var Q106;
            {var subQ0=sQuery(id+"F2.wireOp",EDGE,"E0");Q106=makeQuery(id+"F3.opExtrude","CAP_EDGE",EDGE,{"disambiguationData":[OSD([subQ0]),TDD([makeQuery(id+"F2.imprint","IMPRINT",EDGE,{"disambiguationData":[TD([[makeQuery(id+"F2.imprint","INTERSECT",VERTEX,{"derivedFrom":[subQ0,sQuery(id+"F2.wireOp",EDGE,"E13.11.2")]}),-1.0]])],"derivedFrom":subQ0})])],"isStart":true});}
            var Q107;
            Q107=makeQuery(id+"F3.opExtrude","CAP_EDGE",EDGE,{"disambiguationData":[OSD([sQuery(id+"F2.wireOp",EDGE,"E13.11.2")])],"isStart":true});
            var Q108;
            Q108=makeQuery(id+"F3.opExtrude","CAP_EDGE",EDGE,{"disambiguationData":[OSD([sQuery(id+"F2.wireOp",EDGE,"E13.11.0")])],"isStart":true});
            var Q109;
            {var subQ0=sQuery(id+"F2.wireOp",EDGE,"E0");Q109=makeQuery(id+"F3.opExtrude","CAP_EDGE",EDGE,{"disambiguationData":[OSD([subQ0]),TDD([makeQuery(id+"F2.imprint","IMPRINT",EDGE,{"disambiguationData":[TD([[makeQuery(id+"F2.imprint","INTERSECT",VERTEX,{"derivedFrom":[subQ0,sQuery(id+"F2.wireOp",EDGE,"E13.10.2")]}),-1.0]])],"derivedFrom":subQ0})])],"isStart":true});}
            var Q110;
            Q110=makeQuery(id+"F3.opExtrude","CAP_EDGE",EDGE,{"disambiguationData":[OSD([sQuery(id+"F2.wireOp",EDGE,"E13.10.2")])],"isStart":true});
            var Q111;
            Q111=makeQuery(id+"F3.opExtrude","CAP_EDGE",EDGE,{"disambiguationData":[OSD([sQuery(id+"F2.wireOp",EDGE,"E13.10.0")])],"isStart":true});
            var Q112;
            {var subQ0=sQuery(id+"F2.wireOp",EDGE,"E0");Q112=makeQuery(id+"F3.opExtrude","CAP_EDGE",EDGE,{"disambiguationData":[OSD([subQ0]),TDD([makeQuery(id+"F2.imprint","IMPRINT",EDGE,{"disambiguationData":[TD([[makeQuery(id+"F2.imprint","INTERSECT",VERTEX,{"derivedFrom":[subQ0,sQuery(id+"F2.wireOp",EDGE,"E13.9.2")]}),-1.0]])],"derivedFrom":subQ0})])],"isStart":true});}
            var Q113;
            Q113=makeQuery(id+"F3.opExtrude","CAP_EDGE",EDGE,{"disambiguationData":[OSD([sQuery(id+"F2.wireOp",EDGE,"E13.9.2")])],"isStart":true});
            var Q114;
            Q114=makeQuery(id+"F3.opExtrude","CAP_EDGE",EDGE,{"disambiguationData":[OSD([sQuery(id+"F2.wireOp",EDGE,"E13.9.0")])],"isStart":true});
            var Q115;
            {var subQ0=sQuery(id+"F2.wireOp",EDGE,"E0");Q115=makeQuery(id+"F3.opExtrude","CAP_EDGE",EDGE,{"disambiguationData":[OSD([subQ0]),TDD([makeQuery(id+"F2.imprint","IMPRINT",EDGE,{"disambiguationData":[TD([[makeQuery(id+"F2.imprint","INTERSECT",VERTEX,{"derivedFrom":[subQ0,sQuery(id+"F2.wireOp",EDGE,"E13.8.2")]}),-1.0]])],"derivedFrom":subQ0})])],"isStart":true});}
            var Q116;
            Q116=makeQuery(id+"F3.opExtrude","CAP_EDGE",EDGE,{"disambiguationData":[OSD([sQuery(id+"F2.wireOp",EDGE,"E13.8.2")])],"isStart":true});
            fillet(context, id + "F6", {"entities" : qUnion([Q0, Q1, Q2, Q3, Q4, Q5, Q6, Q7, Q8, Q9, Q10, Q11, Q12, Q13, Q14, Q15, Q16, Q17, Q18, Q19, Q20, Q21, Q22, Q23, Q24, Q25, Q26, Q27, Q28, Q29, Q30, Q31, Q32, Q33, Q34, Q35, Q36, Q37, Q38, Q39, Q40, Q41, Q42, Q43, Q44, Q45, Q46, Q47, Q48, Q49, Q50, Q51, Q52, Q53, Q54, Q55, Q56, Q57, Q58, Q59, Q60, Q61, Q62, Q63, Q64, Q65, Q66, Q67, Q68, Q69, Q70, Q71, Q72, Q73, Q74, Q75, Q76, Q77, Q78, Q79, Q80, Q81, Q82, Q83, Q84, Q85, Q86, Q87, Q88, Q89, Q90, Q91, Q92, Q93, Q94, Q95, Q96, Q97, Q98, Q99, Q100, Q101, Q102, Q103, Q104, Q105, Q106, Q107, Q108, Q109, Q110, Q111, Q112, Q113, Q114, Q115, Q116]), "radius" : (getVariable(context, 'TeethFillet')) * mm, "tangentPropagation" : true, "allowEdgeOverflow" : false});
        }
    });
